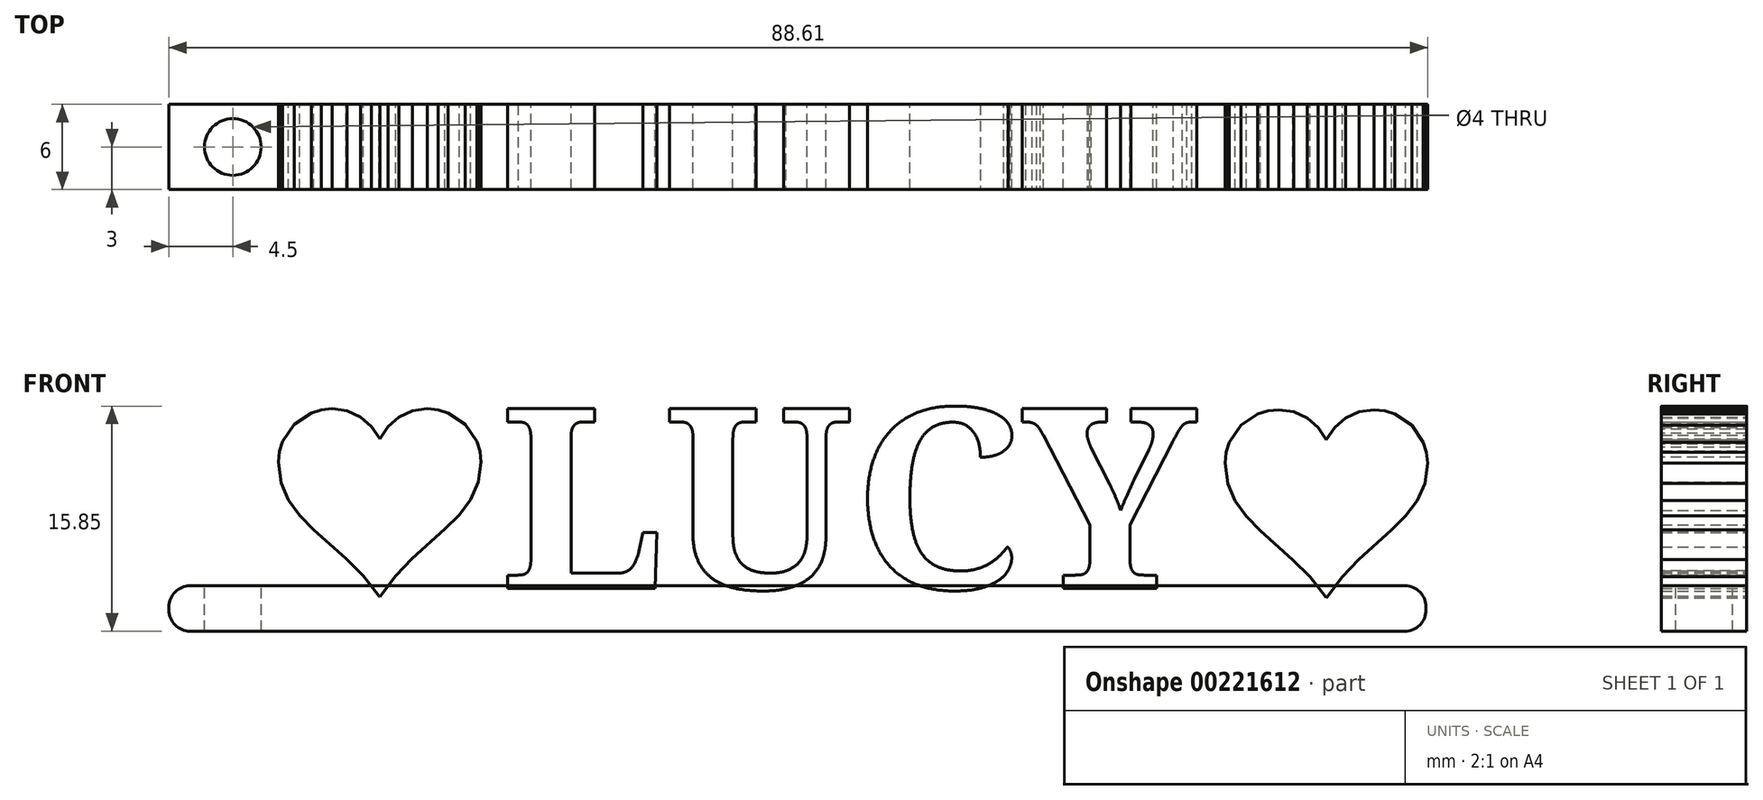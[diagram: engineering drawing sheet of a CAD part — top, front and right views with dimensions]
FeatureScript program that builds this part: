
annotation { "Feature Type Name" : "Feature", "Feature Type Description" : "" }
export const myFeature = defineFeature(function(context is Context, id is Id, definition is map)
    precondition{}
    {
        {
            var Q0;
            Q0=qCreatedBy(makeId("Front.planeOp"),FACE);
            var sketch = newSketch(context, id + "F0", { "sketchPlane" : qUnion([Q0])});
            skText(sketch, "E0", { "text": "   LUCY", "fontName": "NotoSerif-Bold.ttf"});
            skLineSegment(sketch, "E1", {"start": v(50.32, 12.6) * mm, "end": v(49.56, 12.52) * mm});
            skLineSegment(sketch, "E2", {"start": v(49.56, 12.52) * mm, "end": v(48.86, 12.3) * mm});
            skLineSegment(sketch, "E3", {"start": v(48.86, 12.3) * mm, "end": v(47.66, 11.5) * mm});
            skLineSegment(sketch, "E4", {"start": v(47.66, 11.5) * mm, "end": v(46.85, 10.3) * mm});
            skLineSegment(sketch, "E5", {"start": v(46.85, 10.3) * mm, "end": v(46.63, 9.59) * mm});
            skLineSegment(sketch, "E6", {"start": v(46.63, 9.59) * mm, "end": v(46.55, 8.83) * mm});
            skLineSegment(sketch, "E7", {"start": v(46.55, 8.83) * mm, "end": v(46.74, 7.39) * mm});
            skLineSegment(sketch, "E8", {"start": v(46.74, 7.39) * mm, "end": v(47.26, 6.16) * mm});
            skLineSegment(sketch, "E9", {"start": v(47.26, 6.16) * mm, "end": v(48.05, 5.08) * mm});
            skLineSegment(sketch, "E10", {"start": v(48.05, 5.08) * mm, "end": v(49.03, 4.08) * mm});
            skLineSegment(sketch, "E11", {"start": v(49.03, 4.08) * mm, "end": v(51.33, 2.03) * mm});
            skLineSegment(sketch, "E12", {"start": v(51.33, 2.03) * mm, "end": v(52.51, 0.82) * mm});
            skLineSegment(sketch, "E13", {"start": v(52.51, 0.82) * mm, "end": v(53.64, -0.59) * mm});
            skLineSegment(sketch, "E14", {"start": v(53.64, -0.59) * mm, "end": v(53.68, -0.65) * mm});
            skLineSegment(sketch, "E15", {"start": v(53.68, -0.65) * mm, "end": v(53.72, -0.59) * mm});
            skLineSegment(sketch, "E16", {"start": v(53.72, -0.59) * mm, "end": v(54.8, 0.82) * mm});
            skLineSegment(sketch, "E17", {"start": v(54.8, 0.82) * mm, "end": v(55.97, 2.03) * mm});
            skLineSegment(sketch, "E18", {"start": v(55.97, 2.03) * mm, "end": v(58.27, 4.12) * mm});
            skLineSegment(sketch, "E19", {"start": v(58.27, 4.12) * mm, "end": v(59.27, 5.13) * mm});
            skLineSegment(sketch, "E20", {"start": v(59.27, 5.13) * mm, "end": v(60.07, 6.21) * mm});
            skLineSegment(sketch, "E21", {"start": v(60.07, 6.21) * mm, "end": v(60.61, 7.42) * mm});
            skLineSegment(sketch, "E22", {"start": v(60.61, 7.42) * mm, "end": v(60.8, 8.83) * mm});
            skLineSegment(sketch, "E23", {"start": v(60.8, 8.83) * mm, "end": v(60.73, 9.59) * mm});
            skLineSegment(sketch, "E24", {"start": v(60.73, 9.59) * mm, "end": v(60.5, 10.3) * mm});
            skLineSegment(sketch, "E25", {"start": v(60.5, 10.3) * mm, "end": v(59.7, 11.5) * mm});
            skLineSegment(sketch, "E26", {"start": v(59.7, 11.5) * mm, "end": v(58.5, 12.3) * mm});
            skLineSegment(sketch, "E27", {"start": v(58.5, 12.3) * mm, "end": v(57.8, 12.52) * mm});
            skLineSegment(sketch, "E28", {"start": v(57.8, 12.52) * mm, "end": v(57.04, 12.6) * mm});
            skLineSegment(sketch, "E29", {"start": v(57.04, 12.6) * mm, "end": v(55.98, 12.44) * mm});
            skLineSegment(sketch, "E30", {"start": v(55.98, 12.44) * mm, "end": v(55.04, 12.01) * mm});
            skLineSegment(sketch, "E31", {"start": v(55.04, 12.01) * mm, "end": v(54.26, 11.35) * mm});
            skLineSegment(sketch, "E32", {"start": v(54.26, 11.35) * mm, "end": v(53.68, 10.5) * mm});
            skLineSegment(sketch, "E33", {"start": v(53.68, 10.5) * mm, "end": v(53.1, 11.35) * mm});
            skLineSegment(sketch, "E34", {"start": v(53.1, 11.35) * mm, "end": v(52.32, 12.01) * mm});
            skLineSegment(sketch, "E35", {"start": v(52.32, 12.01) * mm, "end": v(51.38, 12.44) * mm});
            skLineSegment(sketch, "E36", {"start": v(51.38, 12.44) * mm, "end": v(50.32, 12.6) * mm});
            skLineSegment(sketch, "E37", {"start": v(45.7, 12.78) * mm, "end": v(74.52, 12.78) * mm, "construction": true});
            skLineSegment(sketch, "E38", {"start": v(-16.32, 12.66) * mm, "end": v(-17.08, 12.59) * mm});
            skLineSegment(sketch, "E39", {"start": v(-17.08, 12.59) * mm, "end": v(-17.78, 12.37) * mm});
            skLineSegment(sketch, "E40", {"start": v(-17.78, 12.37) * mm, "end": v(-18.98, 11.56) * mm});
            skLineSegment(sketch, "E41", {"start": v(-18.98, 11.56) * mm, "end": v(-19.79, 10.36) * mm});
            skLineSegment(sketch, "E42", {"start": v(-19.79, 10.36) * mm, "end": v(-20, 9.65) * mm});
            skLineSegment(sketch, "E43", {"start": v(-20, 9.65) * mm, "end": v(-20.09, 8.9) * mm});
            skLineSegment(sketch, "E44", {"start": v(-20.09, 8.9) * mm, "end": v(-19.9, 7.45) * mm});
            skLineSegment(sketch, "E45", {"start": v(-19.9, 7.45) * mm, "end": v(-19.38, 6.22) * mm});
            skLineSegment(sketch, "E46", {"start": v(-19.38, 6.22) * mm, "end": v(-18.6, 5.15) * mm});
            skLineSegment(sketch, "E47", {"start": v(-18.6, 5.15) * mm, "end": v(-17.6, 4.15) * mm});
            skLineSegment(sketch, "E48", {"start": v(-17.6, 4.15) * mm, "end": v(-15.31, 2.09) * mm});
            skLineSegment(sketch, "E49", {"start": v(-15.31, 2.09) * mm, "end": v(-14.13, 0.89) * mm});
            skLineSegment(sketch, "E50", {"start": v(-14.13, 0.89) * mm, "end": v(-13, -0.52) * mm});
            skLineSegment(sketch, "E51", {"start": v(-13, -0.52) * mm, "end": v(-12.96, -0.59) * mm});
            skLineSegment(sketch, "E52", {"start": v(-12.96, -0.59) * mm, "end": v(-12.92, -0.52) * mm});
            skLineSegment(sketch, "E53", {"start": v(-12.92, -0.52) * mm, "end": v(-11.84, 0.89) * mm});
            skLineSegment(sketch, "E54", {"start": v(-11.84, 0.89) * mm, "end": v(-10.67, 2.1) * mm});
            skLineSegment(sketch, "E55", {"start": v(-10.67, 2.1) * mm, "end": v(-8.37, 4.19) * mm});
            skLineSegment(sketch, "E56", {"start": v(-8.37, 4.19) * mm, "end": v(-7.37, 5.2) * mm});
            skLineSegment(sketch, "E57", {"start": v(-7.37, 5.2) * mm, "end": v(-6.56, 6.28) * mm});
            skLineSegment(sketch, "E58", {"start": v(-6.56, 6.28) * mm, "end": v(-6.03, 7.49) * mm});
            skLineSegment(sketch, "E59", {"start": v(-6.03, 7.49) * mm, "end": v(-5.83, 8.9) * mm});
            skLineSegment(sketch, "E60", {"start": v(-5.83, 8.9) * mm, "end": v(-5.91, 9.65) * mm});
            skLineSegment(sketch, "E61", {"start": v(-5.91, 9.65) * mm, "end": v(-6.13, 10.36) * mm});
            skLineSegment(sketch, "E62", {"start": v(-6.13, 10.36) * mm, "end": v(-6.94, 11.56) * mm});
            skLineSegment(sketch, "E63", {"start": v(-6.94, 11.56) * mm, "end": v(-8.13, 12.37) * mm});
            skLineSegment(sketch, "E64", {"start": v(-8.13, 12.37) * mm, "end": v(-8.84, 12.59) * mm});
            skLineSegment(sketch, "E65", {"start": v(-8.84, 12.59) * mm, "end": v(-9.6, 12.66) * mm});
            skLineSegment(sketch, "E66", {"start": v(-9.6, 12.66) * mm, "end": v(-10.66, 12.5) * mm});
            skLineSegment(sketch, "E67", {"start": v(-10.66, 12.5) * mm, "end": v(-11.6, 12.08) * mm});
            skLineSegment(sketch, "E68", {"start": v(-11.6, 12.08) * mm, "end": v(-12.38, 11.41) * mm});
            skLineSegment(sketch, "E69", {"start": v(-12.38, 11.41) * mm, "end": v(-12.96, 10.56) * mm});
            skLineSegment(sketch, "E70", {"start": v(-12.96, 10.56) * mm, "end": v(-13.54, 11.41) * mm});
            skLineSegment(sketch, "E71", {"start": v(-13.54, 11.41) * mm, "end": v(-14.32, 12.08) * mm});
            skLineSegment(sketch, "E72", {"start": v(-14.32, 12.08) * mm, "end": v(-15.26, 12.5) * mm});
            skLineSegment(sketch, "E73", {"start": v(-15.26, 12.5) * mm, "end": v(-16.32, 12.66) * mm});
            const initialGuessF0  = {"E0": [-0.0183, 0, 1, 0, 0.01278]};
            skSetInitialGuess(sketch, initialGuessF0);
            skSolve(sketch);
        }
        {
            var Q0;
            Q0=qSketchRegion(id+"F0",true);
            extrude(context, id + "F1", {"entities" : qUnion([Q0]), "endBound" : BoundingType.SYMMETRIC, "depth" : 6 * mm});
        }
        {
            var Q0;
            Q0=qCreatedBy(makeId("Top.planeOp"),FACE);
            var sketch = newSketch(context, id + "F2", { "sketchPlane" : qUnion([Q0])});
            skLineSegment(sketch, "E74.bottom", {"start": v(-20.3, 3) * mm, "end": v(60.7, 3) * mm});
            skLineSegment(sketch, "E74.top", {"start": v(-20.3, -3) * mm, "end": v(60.7, -3) * mm});
            skLineSegment(sketch, "E74.left", {"start": v(-20.3, 3) * mm, "end": v(-20.3, -3) * mm});
            skLineSegment(sketch, "E74.right", {"start": v(60.7, 3) * mm, "end": v(60.7, -3) * mm});
            skSolve(sketch);
        }
        {
            var Q0;
            Q0=makeQuery(id+"F2.imprint","IMPRINT",FACE,{"disambiguationData":[TD([[makeQuery(id+"F2.imprint","IMPRINT",EDGE,{"derivedFrom":sQuery(id+"F2.wireOp",EDGE,"E74.bottom")}),-1.0]])]});
            extrude(context, id + "F3", {"entities" : qUnion([Q0]), "depth" : 0.2 * mm});
        }
        {
            var Q0;
            Q0=makeQuery(id+"F3.opExtrude","CAP_FACE",FACE,{"disambiguationData":[OSD([sQuery(id+"F2.wireOp",EDGE,"E74.bottom"),sQuery(id+"F2.wireOp",EDGE,"E74.top"),sQuery(id+"F2.wireOp",EDGE,"E74.left"),sQuery(id+"F2.wireOp",EDGE,"E74.right")])],"isStart":true});
            extrude(context, id + "F4", {"entities" : qUnion([Q0]), "depth" : 3 * mm});
        }
        {
            var Q0;
            {var subQ0=sQuery(id+"F2.wireOp",EDGE,"E74.left");Q0=makeQuery(id+"FaVoHrOpcFZXiYX_6.opBoolean","MERGE",FACE,{"derivedFrom":[makeQuery(id+"F3.opExtrude","SWEPT_FACE",FACE,{"disambiguationData":[OSD([subQ0])]}),makeQuery(id+"F4.opExtrude","SWEPT_FACE",FACE,{"disambiguationData":[OSD([subQ0])]})]});}
            var sketch = newSketch(context, id + "F5", { "sketchPlane" : qUnion([Q0])});
            skLineSegment(sketch, "E75.bottom", {"start": v(-3, -3) * mm, "end": v(3, -3) * mm});
            skLineSegment(sketch, "E75.top", {"start": v(-3, 0.2) * mm, "end": v(3, 0.2) * mm});
            skLineSegment(sketch, "E75.left", {"start": v(-3, -3) * mm, "end": v(-3, 0.2) * mm});
            skLineSegment(sketch, "E75.right", {"start": v(3, -3) * mm, "end": v(3, 0.2) * mm});
            skSolve(sketch);
        }
        {
            var Q0;
            Q0=qSketchRegion(id+"F5",true);
            extrude(context, id + "F6", {"entities" : qUnion([Q0]), "operationType" : NewBodyOperationType.ADD, "depth" : 7.5 * mm});
        }
        {
            var Q0;
            Q0=makeQuery(id+"F6.opExtrude","CAP_EDGE",EDGE,{"disambiguationData":[OSD([sQuery(id+"F5.wireOp",EDGE,"E75.bottom")])],"isStart":false});
            var Q1;
            Q1=makeQuery(id+"F6.opExtrude","CAP_EDGE",EDGE,{"disambiguationData":[OSD([sQuery(id+"F5.wireOp",EDGE,"E75.top")])],"isStart":false});
            var Q2;
            Q2=makeQuery(id+"F4.opExtrude","CAP_EDGE",EDGE,{"disambiguationData":[OSD([sQuery(id+"F2.wireOp",EDGE,"E74.right")])],"isStart":false});
            fillet(context, id + "F7", {"entities" : qUnion([Q0, Q1, Q2]), "radius" : 1.5 * mm, "tangentPropagation" : true, "allowEdgeOverflow" : false});
        }
        {
            var Q0;
            {var subQ19=sQuery(id+"F2.wireOp",EDGE,"E74.top");var subQ20=sQuery(id+"F2.wireOp",EDGE,"E74.bottom");var subQ63=sQuery(id+"F0.wireOp",EDGE,"E0.sketch_text.stroke-2");var subQ66=sQuery(id+"F2.wireOp",EDGE,"E74.left");Q0=makeQuery(id+"F6.boolean.opBoolean","MERGE",FACE,{"derivedFrom":[makeQuery(id+"FaVoHrOpcFZXiYX_6.opBoolean","SPLIT",FACE,{"disambiguationData":[TD([makeQuery(id+"F1.opExtrude","SWEPT_FACE",FACE,{"disambiguationData":[OSD([subQ63])]})])],"derivedFrom":makeQuery(id+"F3.opExtrude","CAP_FACE",FACE,{"disambiguationData":[OSD([subQ20,subQ19,subQ66,sQuery(id+"F2.wireOp",EDGE,"E74.right")])],"isStart":false})}),makeQuery(id+"F6.opExtrude","SWEPT_FACE",FACE,{"disambiguationData":[OSD([sQuery(id+"F5.wireOp",EDGE,"E75.top")])]})]});}
            var sketch = newSketch(context, id + "F8", { "sketchPlane" : qUnion([Q0])});
            skCircle(sketch, "E76", {"center": v(-23.3, 0) * mm, "radius": 2 * mm});
            skSolve(sketch);
        }
        {
            var Q0;
            Q0=makeQuery(id+"F8.imprint","IMPRINT",FACE,{"disambiguationData":[TD([[makeQuery(id+"F8.imprint","IMPRINT",EDGE,{"derivedFrom":sQuery(id+"F8.wireOp",EDGE,"E76")}),1.0]])]});
            extrude(context, id + "F9", {"entities" : qUnion([Q0]), "operationType" : NewBodyOperationType.REMOVE, "oppositeDirection" : true, "depth" : 4 * mm});
        }
        {
            var Q0;
            Q0=makeQuery(id+"F3.opExtrude","CAP_EDGE",EDGE,{"disambiguationData":[OSD([sQuery(id+"F2.wireOp",EDGE,"E74.right")])],"isStart":false});
            fillet(context, id + "F10", {"entities" : qUnion([Q0]), "radius" : 1.5 * mm, "tangentPropagation" : true, "allowEdgeOverflow" : false});
        }
    });
